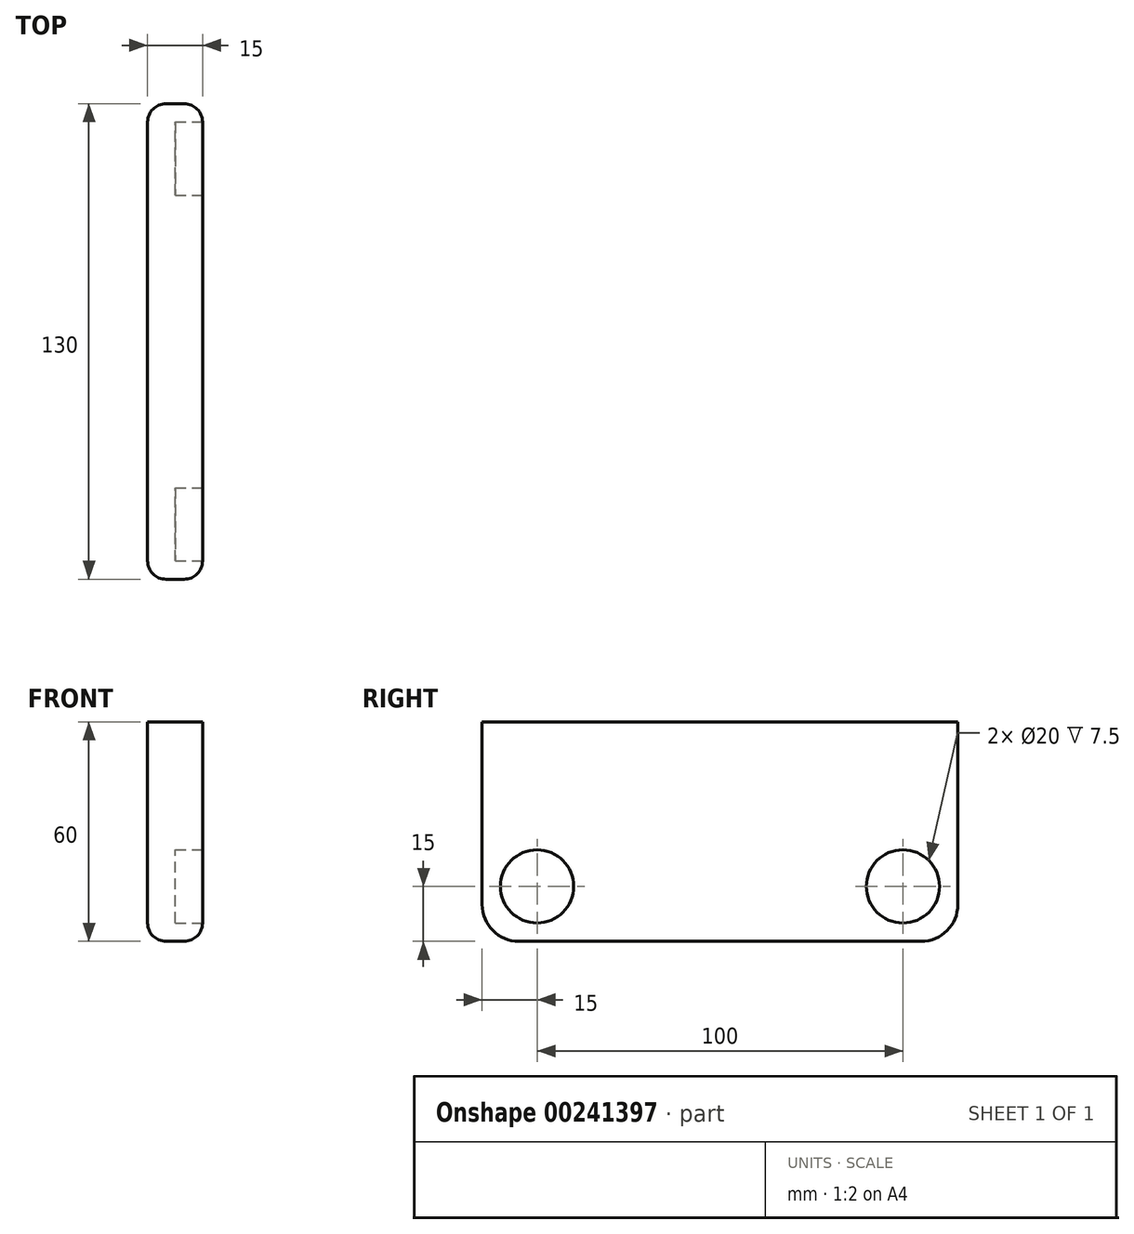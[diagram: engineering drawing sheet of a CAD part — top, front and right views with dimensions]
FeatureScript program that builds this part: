
annotation { "Feature Type Name" : "Feature", "Feature Type Description" : "" }
export const myFeature = defineFeature(function(context is Context, id is Id, definition is map)
    precondition{}
    {
        {
            var Q0;
            Q0=qCreatedBy(makeId("Top.planeOp"),FACE);
            var sketch = newSketch(context, id + "F0", { "sketchPlane" : qUnion([Q0])});
            skLineSegment(sketch, "E0.bottom", {"start": v(-7.5, 65) * mm, "end": v(7.5, 65) * mm});
            skLineSegment(sketch, "E0.top", {"start": v(-7.5, -65) * mm, "end": v(7.5, -65) * mm});
            skLineSegment(sketch, "E0.left", {"start": v(-7.5, 65) * mm, "end": v(-7.5, -65) * mm});
            skLineSegment(sketch, "E0.right", {"start": v(7.5, 65) * mm, "end": v(7.5, -65) * mm});
            skPoint(sketch, "E0.middle", {"position": v(0, 0) * mm});
            skSolve(sketch);
        }
        {
            var Q0;
            Q0 = qSketchRegion(id + "F0", true);
            extrude(context, id + "F1", {"entities" : qUnion([Q0]), "depth" : 60 * mm});
        }
        {
            var Q0;
            Q0=makeQuery(id+"F1.opExtrude","SWEPT_FACE",FACE,{"disambiguationData":[OSD([sQuery(id+"F0.wireOp",EDGE,"E0.right")])]});
            var sketch = newSketch(context, id + "F2", { "sketchPlane" : qUnion([Q0])});
            skCircle(sketch, "E1", {"center": v(-50, 15) * mm, "radius": 10 * mm});
            skCircle(sketch, "E2", {"center": v(50, 15) * mm, "radius": 10 * mm});
            skSolve(sketch);
        }
        {
            var Q0;
            Q0 = qSketchRegion(id + "F2", true);
            extrude(context, id + "F3", {"entities" : qUnion([Q0]), "operationType" : NewBodyOperationType.REMOVE, "oppositeDirection" : true, "depth" : 7.5 * mm});
        }
        {
            var Q0;
            Q0=makeQuery(id+"F1.opExtrude","CAP_EDGE",EDGE,{"disambiguationData":[OSD([sQuery(id+"F0.wireOp",EDGE,"E0.top")])],"isStart":true});
            var Q1;
            Q1=makeQuery(id+"F1.opExtrude","CAP_EDGE",EDGE,{"disambiguationData":[OSD([sQuery(id+"F0.wireOp",EDGE,"E0.bottom")])],"isStart":true});
            fillet(context, id + "F4", {"entities" : qUnion([Q0, Q1]), "radius" : 10 * mm, "allowEdgeOverflow" : false});
        }
        {
            var Q0;
            Q0=makeQuery(id+"F1.opExtrude","CAP_EDGE",EDGE,{"disambiguationData":[OSD([sQuery(id+"F0.wireOp",EDGE,"E0.right")])],"isStart":true});
            var Q1;
            Q1=makeQuery(id+"F1.opExtrude","CAP_EDGE",EDGE,{"disambiguationData":[OSD([sQuery(id+"F0.wireOp",EDGE,"E0.left")])],"isStart":true});
            fillet(context, id + "F5", {"entities" : qUnion([Q0, Q1]), "radius" : 5 * mm, "tangentPropagation" : true, "allowEdgeOverflow" : false});
        }
    });
